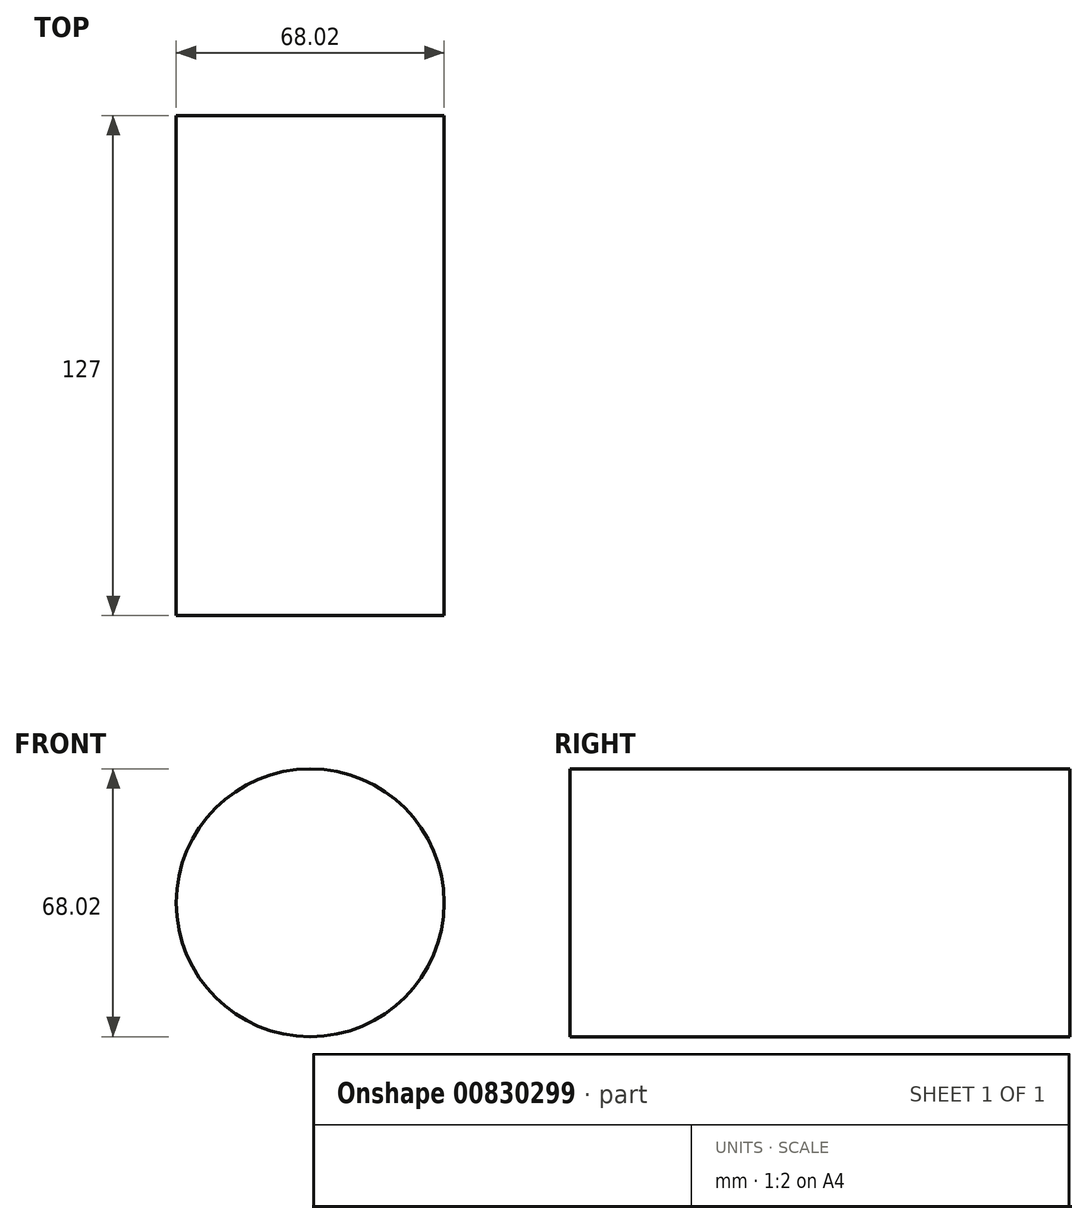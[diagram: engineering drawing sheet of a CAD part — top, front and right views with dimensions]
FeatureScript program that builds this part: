
annotation { "Feature Type Name" : "Feature", "Feature Type Description" : "" }
export const myFeature = defineFeature(function(context is Context, id is Id, definition is map)
    precondition{}
    {
        {
            var Q0;
            Q0=qCreatedBy(makeId("Front.planeOp"),FACE);
            var sketch = newSketch(context, id + "F0", { "sketchPlane" : qUnion([Q0])});
            skCircle(sketch, "E0", {"center": v(0, 0) * mm, "radius": 34.01 * mm});
            skSolve(sketch);
        }
        {
            var Q0;
            Q0=sQuery(id+"F0.wireOp",EDGE,"E0");
            extrude(context, id + "F1", {"bodyType" : ToolBodyType.SURFACE, "surfaceEntities" : qUnion([Q0]), "depth" : 127 * mm, "offsetDistance" : 25.4 * mm});
        }
    });
